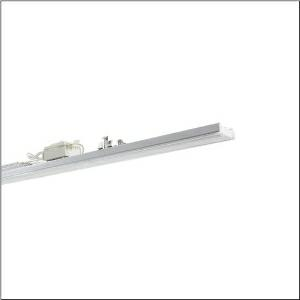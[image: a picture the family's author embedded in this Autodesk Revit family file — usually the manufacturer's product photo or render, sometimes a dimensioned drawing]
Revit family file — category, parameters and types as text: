
# Revit family: licross_r__21_recessed_ho_52tl11de47xs_6da4
name_source: partatom
category: Lighting Fixtures
units: mm (PartAtom-declared; Revit-internal decimal feet)

## family parameters
Cut with Voids When Loaded = No
Host = Face
Light Source = No
Part Type = Normal
Room Calculation Point = No
Round Connector Dimension = Use Diameter
Shared = No

## types (1)
- --- (1 x LED, 7480 lm, 44.1 W, 4000K)
    Apparent Load = 44 VA
    CIE Flux Codes = 87 95 99 100 100
    Color Rendering = 80
    Color Temperature = 4000K
    Default Elevation = 1800 mm
    Description = Licross® 21 Recessed HO, luminaire insert, of sheet steel, galvanised, coil coated, white, length: 750mm, width: 66mm, height: 67mm, LED rated luminous flux: 7.480lm, light colour: 840, control gear: DALI 2, with plug, 5-pole, with phase selection, mains connection: 220..240V, AC, 50/60Hz, rated input power: 44W, halogen-free wiring, primary light control with lens, of plastic, primary optical cover: cover, of PMMA, light emission: direct distribution, primary light characteristic: symmetric, protection rating (complete): IP40, insulation class (complete): insulation class I (protective earthing), certification: CE, ENEC, VDE, UKCA, protection symbol: D if used in an environment without relevant dust loads with corresponding accessories, impact resistance: IK06, permissible ambient temperature for indoor applications: -25..+30°C, corresponds to IFS (International Featured Standards) requirements for safety and quality in the food industry, reducing of maximum allowable ambient temperature of 5°C with ceiling mounting, LABS conformity tested according to VDMA 24364:2018-05, packaging unit: 1 piece
    Height = 58 mm
    Lamp = 1 x LED
    Lamp Light Flux = 7480 lm
    Lamp Power = 44.1 W
    Lamp count = 1
    Length = 750 mm
    Luminous efficacy = 170 lm/W
    Manufacturer = Siteco
    ModVariant = No
    Model = 52TL11DE47XS
    Mounting Place = Ceiling
    Mounting Type = Pendant
    Number of Poles = 1
    OnlyDefault = Yes
    Power Factor = 1
    Product Name = Licross® 21 Recessed HO
    Product group = luminaire insert
    ProductGroupID = 902
    Protection Class = Protection class I
    Protection Degree = IP 40
    RLX_Detail_Level = 1
    RLX_Emergency_Light_Flux = 0 lm
    RLX_Emergency_Type = 0
    RLX_Emergency_Type_DB = No
    RlxData = <blob elided: 29177 chars, md5=810f5f22>
    Socket = socket
    Standby Power = 0 W
    System Light Flux = 7480 lm
    System Power = 44 W
    Type Comments = factory setting: luminous flux: 100 % | dim-lin: 254 | 484 mA
    Type Image = l_1296930.jpg
    URL = http://relux.com
    VarID = @adj_127462
    Voltage = 0 V
    Weight = 0.00 kg
    Width = 66 mm

## geometry (parser evidence)
native form markers: Blend x4, Sweep x8
no freeform markers — native parametric forms only
